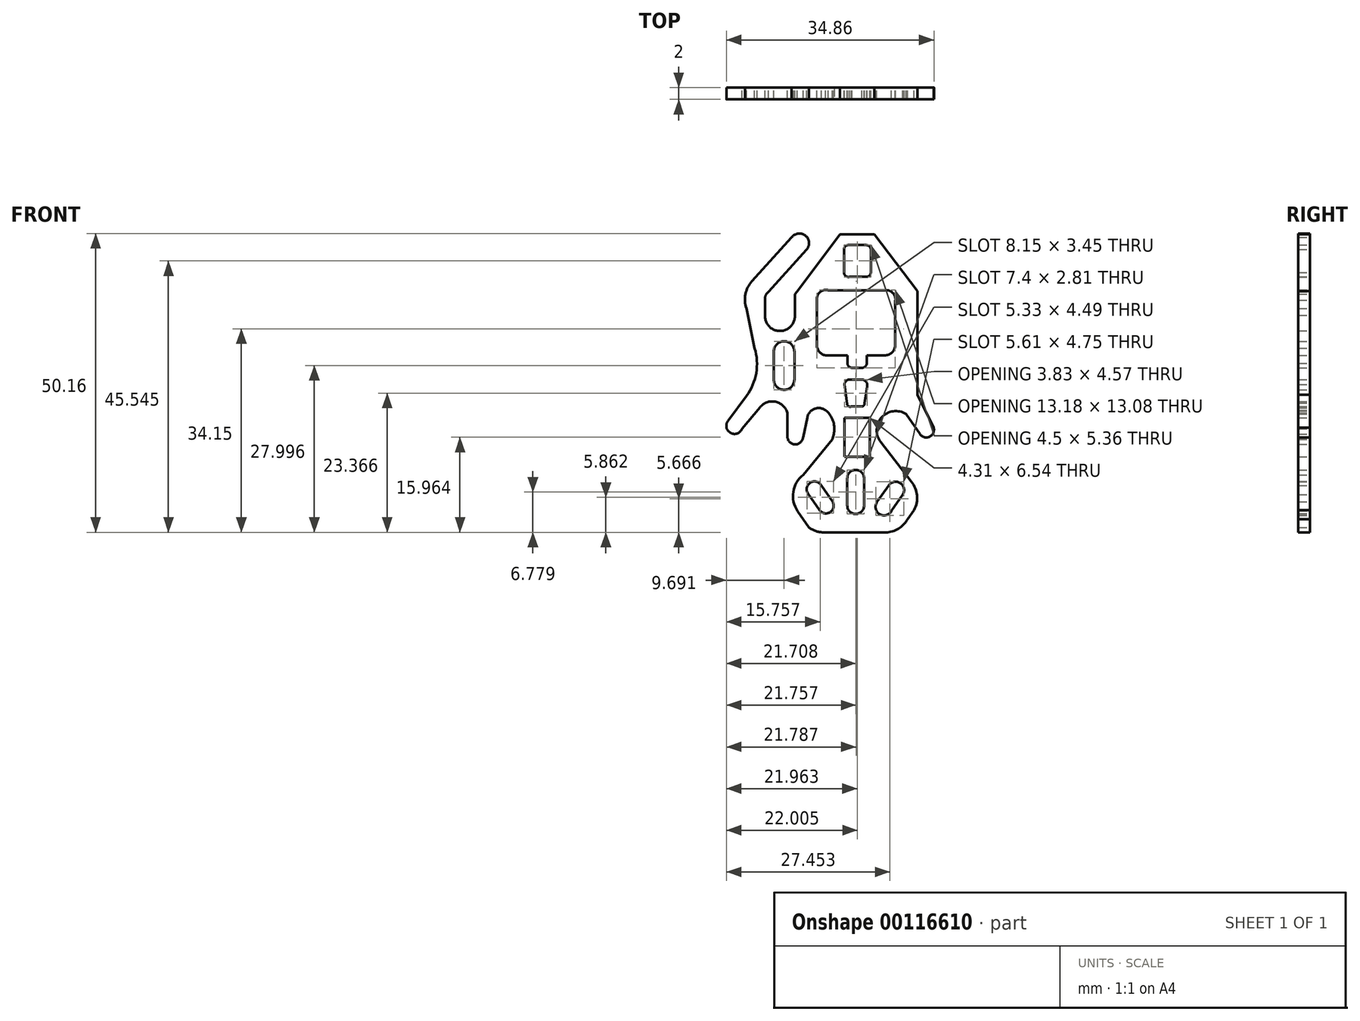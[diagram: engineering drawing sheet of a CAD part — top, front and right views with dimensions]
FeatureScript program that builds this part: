
annotation { "Feature Type Name" : "Feature", "Feature Type Description" : "" }
export const myFeature = defineFeature(function(context is Context, id is Id, definition is map)
    precondition{}
    {
        {
            var Q0;
            Q0=qCreatedBy(makeId("Front.planeOp"),FACE);
            var sketch = newSketch(context, id + "F0", { "sketchPlane" : qUnion([Q0])});
            skLineSegment(sketch, "E0", {"start": v(5.41, 14.79) * mm, "end": v(12.57, 24.35) * mm});
            skLineSegment(sketch, "E1", {"start": v(12.57, 24.35) * mm, "end": v(18.38, 24.35) * mm});
            skLineSegment(sketch, "E2", {"start": v(18.38, 24.35) * mm, "end": v(25.6, 14.85) * mm});
            skLineSegment(sketch, "E3", {"start": v(25.6, 14.85) * mm, "end": v(25.6, -2.58) * mm});
            skLineSegment(sketch, "E4", {"start": v(25.6, -2.58) * mm, "end": v(28.33, -8.1) * mm});
            skLineSegment(sketch, "E5", {"start": v(9.75, -25.65) * mm, "end": v(20.29, -25.65) * mm});
            skLineSegment(sketch, "E6", {"start": v(23.94, -23.44) * mm, "end": v(25.06, -21.91) * mm});
            skLineSegment(sketch, "E7", {"start": v(5.5, -22.1) * mm, "end": v(7.4, -24.82) * mm});
            skLineSegment(sketch, "E8", {"start": v(6.44, -16) * mm, "end": v(11.31, -10.02) * mm});
            skLineSegment(sketch, "E9", {"start": v(7.11, -6.34) * mm, "end": v(6.4, -9.69) * mm});
            skLineSegment(sketch, "E10", {"start": v(3.77, -9.57) * mm, "end": v(3.77, -5.58) * mm});
            skLineSegment(sketch, "E11", {"start": v(1.48, 0) * mm, "end": v(1.48, 4.7) * mm});
            skLineSegment(sketch, "E12", {"start": v(4.94, 0) * mm, "end": v(4.94, 4.7) * mm});
            skLineSegment(sketch, "E13", {"start": v(-6.21, -6.95) * mm, "end": v(-3.1, -2.76) * mm});
            skLineSegment(sketch, "E14", {"start": v(-3.94, -8.38) * mm, "end": v(-0.84, -4.63) * mm});
            skArc(sketch, "E15", {"start": v(9.75, -25.65) * mm, "mid": v(8.5, -25.43) * mm, "end": v(7.4, -24.82) * mm});
            skArc(sketch, "E16", {"start": v(20.29, -25.65) * mm, "mid": v(22.42, -25.05) * mm, "end": v(23.94, -23.44) * mm});
            skArc(sketch, "E17", {"start": v(5.5, -22.1) * mm, "mid": v(4.75, -18.86) * mm, "end": v(6.44, -16) * mm});
            skLineSegment(sketch, "E18", {"start": v(23.7, -5.8) * mm, "end": v(26.03, -9.17) * mm});
            skArc(sketch, "E19", {"start": v(26.03, -9.17) * mm, "mid": v(27.63, -9.6) * mm, "end": v(28.33, -8.1) * mm});
            skLineSegment(sketch, "E20", {"start": v(19.44, -10.5) * mm, "end": v(24.6, -17.14) * mm});
            skArc(sketch, "E21", {"start": v(24.6, -17.14) * mm, "mid": v(25.53, -19.46) * mm, "end": v(25.06, -21.91) * mm});
            skArc(sketch, "E22", {"start": v(1.48, 4.7) * mm, "mid": v(3.21, 6.42) * mm, "end": v(4.94, 4.7) * mm});
            skArc(sketch, "E23", {"start": v(1.48, 0) * mm, "mid": v(3.21, -1.73) * mm, "end": v(4.94, 0) * mm});
            skArc(sketch, "E24", {"start": v(-6.21, -6.95) * mm, "mid": v(-5.77, -8.97) * mm, "end": v(-3.83, -8.24) * mm});
            skArc(sketch, "E25", {"start": v(-0.84, -4.63) * mm, "mid": v(1.75, -3.72) * mm, "end": v(3.77, -5.58) * mm});
            skArc(sketch, "E26", {"start": v(3.77, -9.57) * mm, "mid": v(5.03, -10.89) * mm, "end": v(6.4, -9.69) * mm});
            skArc(sketch, "E27", {"start": v(7.11, -6.34) * mm, "mid": v(8.32, -4.92) * mm, "end": v(10.17, -5.14) * mm});
            skLineSegment(sketch, "E28", {"start": v(13.82, -16.58) * mm, "end": v(13.82, -21.17) * mm});
            skLineSegment(sketch, "E29", {"start": v(16.63, -21.17) * mm, "end": v(16.63, -16.58) * mm});
            skArc(sketch, "E30", {"start": v(13.82, -16.58) * mm, "mid": v(15.23, -15.17) * mm, "end": v(16.63, -16.58) * mm});
            skArc(sketch, "E31", {"start": v(13.82, -21.17) * mm, "mid": v(15.23, -22.57) * mm, "end": v(16.63, -21.17) * mm});
            skLineSegment(sketch, "E32", {"start": v(7.24, -19.16) * mm, "end": v(9.16, -21.92) * mm});
            skLineSegment(sketch, "E33", {"start": v(11.36, -20.52) * mm, "end": v(9.46, -17.79) * mm});
            skArc(sketch, "E34", {"start": v(7.24, -19.16) * mm, "mid": v(7.62, -17.3) * mm, "end": v(9.46, -17.79) * mm});
            skArc(sketch, "E35", {"start": v(9.16, -21.92) * mm, "mid": v(10.93, -22.27) * mm, "end": v(11.36, -20.52) * mm});
            skLineSegment(sketch, "E36", {"start": v(20.78, -17.76) * mm, "end": v(18.83, -20.55) * mm});
            skLineSegment(sketch, "E37", {"start": v(23.15, -19.33) * mm, "end": v(21.26, -22.04) * mm});
            skArc(sketch, "E38", {"start": v(18.83, -20.55) * mm, "mid": v(19.25, -22.6) * mm, "end": v(21.26, -22.04) * mm});
            skArc(sketch, "E39", {"start": v(20.78, -17.76) * mm, "mid": v(22.73, -17.4) * mm, "end": v(23.15, -19.33) * mm});
            skFitSpline(sketch, "E40", {"points": [v(11.31, -10.02) * mm, v(11.6, -7.6) * mm, v(10.17, -5.14) * mm], "startDerivative": vector(1.7, 5.08) * mm, "endDerivative": vector(-4.05, 2.58) * mm});
            skLineSegment(sketch, "E41", {"start": v(-1.74, 5.28) * mm, "end": v(-3.12, 11.94) * mm});
            skLineSegment(sketch, "E42", {"start": v(-2.19, 16.48) * mm, "end": v(4.47, 23.83) * mm});
            skLineSegment(sketch, "E43", {"start": v(7, 21.8) * mm, "end": v(0.58, 14.7) * mm});
            skLineSegment(sketch, "E44", {"start": v(0, 13.57) * mm, "end": v(0, 10.66) * mm});
            skLineSegment(sketch, "E45", {"start": v(5.02, 10.76) * mm, "end": v(5.02, 14.36) * mm});
            skLineSegment(sketch, "E46", {"start": v(5.02, 14.36) * mm, "end": v(5.41, 14.79) * mm});
            skLineSegment(sketch, "E47", {"start": v(10.6, 15) * mm, "end": v(20.36, 15) * mm});
            skLineSegment(sketch, "E48", {"start": v(21.9, 13.32) * mm, "end": v(21.9, 5.87) * mm});
            skLineSegment(sketch, "E49", {"start": v(20.07, 4.04) * mm, "end": v(17.1, 4.04) * mm});
            skLineSegment(sketch, "E50", {"start": v(17.1, 4.04) * mm, "end": v(17.1, 2.71) * mm});
            skLineSegment(sketch, "E51", {"start": v(13.85, 2.76) * mm, "end": v(13.85, 4.04) * mm});
            skLineSegment(sketch, "E52", {"start": v(13.85, 4.04) * mm, "end": v(10.15, 4.04) * mm});
            skLineSegment(sketch, "E53", {"start": v(8.72, 5.77) * mm, "end": v(8.72, 13.52) * mm});
            skArc(sketch, "E54", {"start": v(0, 13.57) * mm, "mid": v(0.15, 14.2) * mm, "end": v(0.58, 14.7) * mm});
            skArc(sketch, "E55", {"start": v(7, 21.8) * mm, "mid": v(6.8, 24.15) * mm, "end": v(4.47, 23.83) * mm});
            skArc(sketch, "E56", {"start": v(-2.19, 16.48) * mm, "mid": v(-3.28, 14.34) * mm, "end": v(-3.12, 11.94) * mm});
            skArc(sketch, "E57", {"start": v(0, 10.66) * mm, "mid": v(2.56, 8.15) * mm, "end": v(5.02, 10.76) * mm});
            skArc(sketch, "E58", {"start": v(8.72, 13.52) * mm, "mid": v(9.3, 14.71) * mm, "end": v(10.6, 15) * mm});
            skArc(sketch, "E59", {"start": v(8.72, 5.77) * mm, "mid": v(9.12, 4.65) * mm, "end": v(10.15, 4.04) * mm});
            skLineSegment(sketch, "E60", {"start": v(14.6, 1.96) * mm, "end": v(16.28, 1.96) * mm});
            skArc(sketch, "E61", {"start": v(20.07, 4.04) * mm, "mid": v(21.36, 4.58) * mm, "end": v(21.9, 5.87) * mm});
            skArc(sketch, "E62", {"start": v(13.85, 2.76) * mm, "mid": v(14.07, 2.21) * mm, "end": v(14.6, 1.96) * mm});
            skArc(sketch, "E63", {"start": v(16.28, 1.96) * mm, "mid": v(16.84, 2.18) * mm, "end": v(17.1, 2.71) * mm});
            skLineSegment(sketch, "E64", {"start": v(13.36, -0.84) * mm, "end": v(13.78, -4.1) * mm});
            skLineSegment(sketch, "E65", {"start": v(16.74, -3.95) * mm, "end": v(17.18, -1.16) * mm});
            skLineSegment(sketch, "E66", {"start": v(14.22, 0) * mm, "end": v(16.3, 0) * mm});
            skLineSegment(sketch, "E67", {"start": v(14.5, -4.53) * mm, "end": v(16.21, -4.53) * mm});
            skArc(sketch, "E68", {"start": v(14.22, 0) * mm, "mid": v(13.62, -0.24) * mm, "end": v(13.36, -0.84) * mm});
            skArc(sketch, "E69", {"start": v(13.78, -4.1) * mm, "mid": v(14.04, -4.5) * mm, "end": v(14.5, -4.53) * mm});
            skArc(sketch, "E70", {"start": v(16.21, -4.53) * mm, "mid": v(16.6, -4.36) * mm, "end": v(16.74, -3.95) * mm});
            skArc(sketch, "E71", {"start": v(17.18, -1.16) * mm, "mid": v(16.99, -0.4) * mm, "end": v(16.3, 0) * mm});
            skArc(sketch, "E72", {"start": v(20.36, 15) * mm, "mid": v(21.5, 14.5) * mm, "end": v(21.9, 13.32) * mm});
            skArc(sketch, "E73", {"start": v(-3.1, -2.76) * mm, "mid": v(-1.46, 1.1) * mm, "end": v(-1.74, 5.28) * mm});
            skLineSegment(sketch, "E74", {"start": v(13.28, 21.83) * mm, "end": v(13.28, 17.96) * mm});
            skLineSegment(sketch, "E75", {"start": v(17.78, 17.96) * mm, "end": v(17.78, 21.83) * mm});
            skLineSegment(sketch, "E76", {"start": v(14.16, 17.23) * mm, "end": v(17.03, 17.23) * mm});
            skArc(sketch, "E77", {"start": v(14.16, 22.56) * mm, "mid": v(13.54, 22.4) * mm, "end": v(13.28, 21.83) * mm});
            skArc(sketch, "E78", {"start": v(13.28, 17.96) * mm, "mid": v(13.54, 17.39) * mm, "end": v(14.16, 17.23) * mm});
            skArc(sketch, "E79", {"start": v(17.03, 17.23) * mm, "mid": v(17.55, 17.44) * mm, "end": v(17.78, 17.96) * mm});
            skLineSegment(sketch, "E80", {"start": v(14.16, 22.56) * mm, "end": v(17.03, 22.56) * mm});
            skArc(sketch, "E81", {"start": v(17.03, 22.56) * mm, "mid": v(17.55, 22.35) * mm, "end": v(17.78, 21.83) * mm});
            skLineSegment(sketch, "E82.bottom", {"start": v(13.33, -12.96) * mm, "end": v(17.64, -12.96) * mm});
            skLineSegment(sketch, "E82.top", {"start": v(13.33, -6.42) * mm, "end": v(17.64, -6.42) * mm});
            skLineSegment(sketch, "E82.left", {"start": v(13.33, -12.96) * mm, "end": v(13.33, -6.42) * mm});
            skLineSegment(sketch, "E82.right", {"start": v(17.64, -12.96) * mm, "end": v(17.64, -6.42) * mm});
            skArc(sketch, "E83", {"start": v(23.7, -5.8) * mm, "mid": v(19.6, -6.35) * mm, "end": v(19.44, -10.5) * mm});
            skSolve(sketch);
        }
        {
            var Q0;
            Q0=makeQuery(id+"F0.imprint","IMPRINT",FACE,{"disambiguationData":[TD([[makeQuery(id+"F0.imprint","IMPRINT",EDGE,{"derivedFrom":sQuery(id+"F0.wireOp",EDGE,"E0")}),-1.0]])]});
            extrude(context, id + "F1", {"entities" : qUnion([Q0]), "depth" : 2 * mm, "symmetric" : true});
        }
    });
